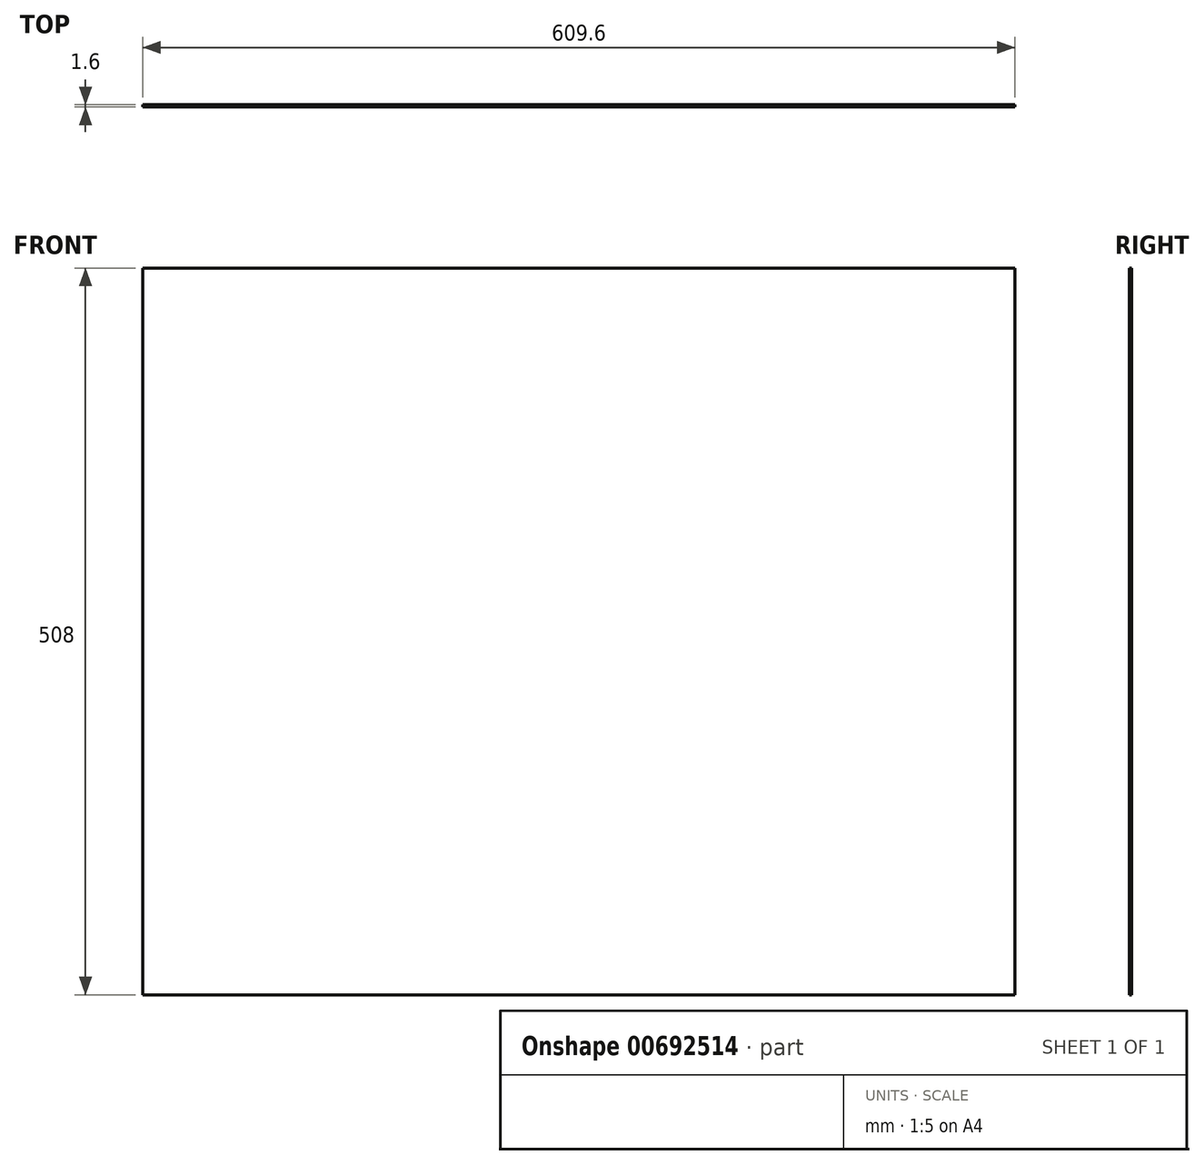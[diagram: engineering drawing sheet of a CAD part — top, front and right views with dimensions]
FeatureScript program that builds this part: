
annotation { "Feature Type Name" : "Feature", "Feature Type Description" : "" }
export const myFeature = defineFeature(function(context is Context, id is Id, definition is map)
    precondition{}
    {
        {
            var Q0;
            Q0=qCreatedBy(makeId("Front.planeOp"),FACE);
            var sketch = newSketch(context, id + "F0", { "sketchPlane" : qUnion([Q0])});
            skLineSegment(sketch, "E0.bottom", {"start": v(-271.78, 265.56) * mm, "end": v(337.82, 265.56) * mm});
            skLineSegment(sketch, "E0.top", {"start": v(-271.78, -242.44) * mm, "end": v(337.82, -242.44) * mm});
            skLineSegment(sketch, "E0.left", {"start": v(-271.78, 265.56) * mm, "end": v(-271.78, -242.44) * mm});
            skLineSegment(sketch, "E0.right", {"start": v(337.82, 265.56) * mm, "end": v(337.82, -242.44) * mm});
            skSolve(sketch);
        }
        {
            var Q0;
            Q0=makeQuery(id+"F0.imprint","IMPRINT",FACE,{"disambiguationData":[TD([[makeQuery(id+"F0.imprint","IMPRINT",EDGE,{"derivedFrom":sQuery(id+"F0.wireOp",EDGE,"E0.bottom")}),-1.0]])]});
            extrude(context, id + "F1", {"entities" : qUnion([Q0]), "endBound" : BoundingType.SYMMETRIC, "depth" : 1.6 * mm, "offsetDistance" : 25.4 * mm});
        }
    });
